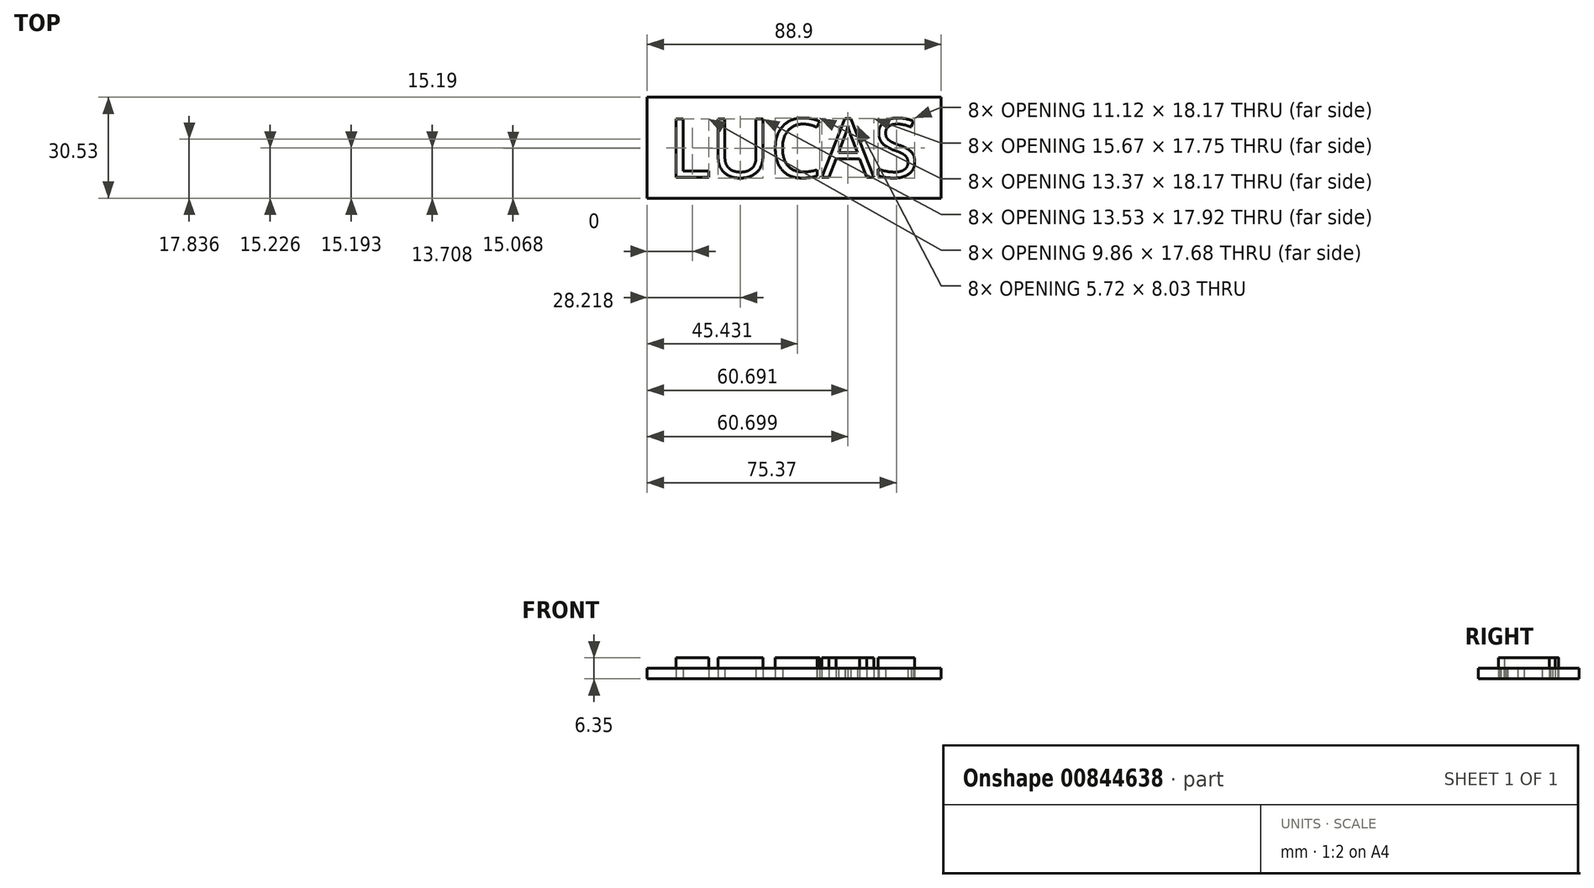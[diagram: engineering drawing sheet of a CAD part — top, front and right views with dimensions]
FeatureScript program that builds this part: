
annotation { "Feature Type Name" : "Feature", "Feature Type Description" : "" }
export const myFeature = defineFeature(function(context is Context, id is Id, definition is map)
    precondition{}
    {
        {
            var Q0;
            Q0=qCreatedBy(makeId("Top.planeOp"),FACE);
            var sketch = newSketch(context, id + "F0", { "sketchPlane" : qUnion([Q0])});
            skText(sketch, "E0", { "text": "LUCAS", "fontName": "OpenSans-Regular.ttf"});
            skLineSegment(sketch, "E1.bottom", {"start": v(-6.35, 6.35) * mm, "end": v(82.55, 6.35) * mm});
            skLineSegment(sketch, "E1.top", {"start": v(-6.35, -24.18) * mm, "end": v(82.55, -24.18) * mm});
            skLineSegment(sketch, "E1.left", {"start": v(-6.35, 6.35) * mm, "end": v(-6.35, -24.18) * mm});
            skLineSegment(sketch, "E1.right", {"start": v(82.55, 6.35) * mm, "end": v(82.55, -24.18) * mm});
            const initialGuessF0  = {"E0": [0, -0.01783, 1, 0, 0.01783]};
            skSetInitialGuess(sketch, initialGuessF0);
            skSolve(sketch);
        }
        {
            var Q0;
            Q0=makeQuery(id+"F0.imprint","IMPRINT",FACE,{"disambiguationData":[TD([[makeQuery(id+"F0.imprint","IMPRINT",EDGE,{"derivedFrom":sQuery(id+"F0.wireOp",EDGE,"E0.sketch_text.stroke-0")}),-1.0]])]});
            var Q1;
            Q1=makeQuery(id+"F0.imprint","IMPRINT",FACE,{"disambiguationData":[TD([[makeQuery(id+"F0.imprint","IMPRINT",EDGE,{"derivedFrom":sQuery(id+"F0.wireOp",EDGE,"E0.sketch_text.stroke-6")}),-1.0]])]});
            var Q2;
            Q2=makeQuery(id+"F0.imprint","IMPRINT",FACE,{"disambiguationData":[TD([[makeQuery(id+"F0.imprint","IMPRINT",EDGE,{"derivedFrom":sQuery(id+"F0.wireOp",EDGE,"E0.sketch_text.stroke-20")}),-1.0]])]});
            var Q3;
            Q3=makeQuery(id+"F0.imprint","IMPRINT",FACE,{"disambiguationData":[TD([[makeQuery(id+"F0.imprint","IMPRINT",EDGE,{"derivedFrom":sQuery(id+"F0.wireOp",EDGE,"E0.sketch_text.stroke-35")}),-1.0]])]});
            var Q4;
            Q4=makeQuery(id+"F0.imprint","IMPRINT",FACE,{"disambiguationData":[TD([[makeQuery(id+"F0.imprint","IMPRINT",EDGE,{"derivedFrom":sQuery(id+"F0.wireOp",EDGE,"E0.sketch_text.stroke-48")}),-1.0]])]});
            extrude(context, id + "F1", {"entities" : qUnion([Q0, Q1, Q2, Q3, Q4]), "depth" : 6.35 * mm, "offsetDistance" : 25 * mm});
        }
        {
            var Q0;
            Q0=makeQuery(id+"F0.imprint","IMPRINT",FACE,{"disambiguationData":[TD([[makeQuery(id+"F0.imprint","IMPRINT",EDGE,{"derivedFrom":sQuery(id+"F0.wireOp",EDGE,"E0.sketch_text.stroke-0")}),1.0]])]});
            var Q1;
            Q1=makeQuery(id+"F0.imprint","IMPRINT",FACE,{"disambiguationData":[TD([[makeQuery(id+"F0.imprint","IMPRINT",EDGE,{"derivedFrom":sQuery(id+"F0.wireOp",EDGE,"E0.sketch_text.stroke-43")}),1.0]])]});
            extrude(context, id + "F2", {"entities" : qUnion([Q0, Q1]), "depth" : 3.17 * mm, "offsetDistance" : 25 * mm});
        }
    });
